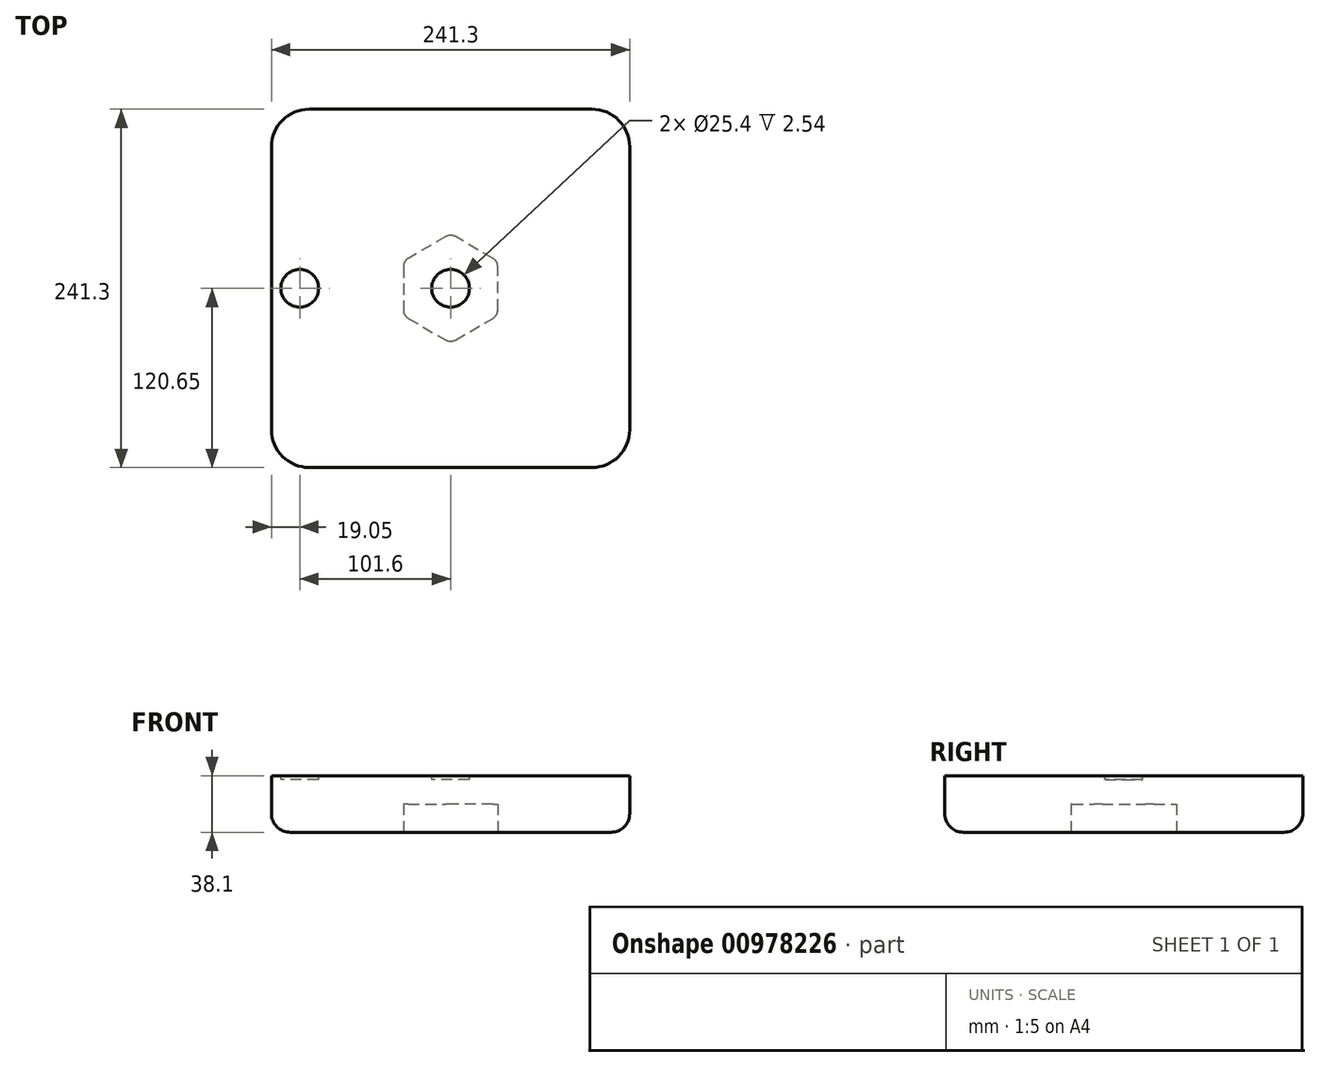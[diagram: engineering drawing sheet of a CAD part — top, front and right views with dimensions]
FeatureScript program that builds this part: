
annotation { "Feature Type Name" : "Feature", "Feature Type Description" : "" }
export const myFeature = defineFeature(function(context is Context, id is Id, definition is map)
    precondition{}
    {
        {
            var Q0;
            Q0=qCreatedBy(makeId("Top.planeOp"),FACE);
            var sketch = newSketch(context, id + "F0", { "sketchPlane" : qUnion([Q0])});
            skLineSegment(sketch, "E0.bottom", {"start": v(-120.65, 120.65) * mm, "end": v(120.65, 120.65) * mm});
            skLineSegment(sketch, "E0.top", {"start": v(-120.65, -120.65) * mm, "end": v(120.65, -120.65) * mm});
            skLineSegment(sketch, "E0.left", {"start": v(-120.65, 120.65) * mm, "end": v(-120.65, -120.65) * mm});
            skLineSegment(sketch, "E0.right", {"start": v(120.65, 120.65) * mm, "end": v(120.65, -120.65) * mm});
            skLineSegment(sketch, "E1", {"start": v(0, 0) * mm, "end": v(0, 120.65) * mm, "construction": true});
            skLineSegment(sketch, "E2", {"start": v(0, 0) * mm, "end": v(120.65, 0) * mm, "construction": true});
            skSolve(sketch);
        }
        {
            var Q0;
            Q0=makeQuery(id+"F0.imprint","IMPRINT",FACE,{"disambiguationData":[TD([[makeQuery(id+"F0.imprint","IMPRINT",EDGE,{"derivedFrom":sQuery(id+"F0.wireOp",EDGE,"E0.bottom")}),-1.0]])]});
            extrude(context, id + "F1", {"entities" : qUnion([Q0]), "oppositeDirection" : true, "depth" : 38.1 * mm, "offsetDistance" : 25.4 * mm});
        }
        {
            var Q0;
            Q0=makeQuery(id+"F1.opExtrude","SWEPT_EDGE",EDGE,{"disambiguationData":[OSD([sQuery(id+"F0.wireOp",EDGE,"E0.top"),sQuery(id+"F0.wireOp",EDGE,"E0.left")])]});
            var Q1;
            Q1=makeQuery(id+"F1.opExtrude","SWEPT_EDGE",EDGE,{"disambiguationData":[OSD([sQuery(id+"F0.wireOp",EDGE,"E0.bottom"),sQuery(id+"F0.wireOp",EDGE,"E0.left")])]});
            var Q2;
            Q2=makeQuery(id+"F1.opExtrude","SWEPT_EDGE",EDGE,{"disambiguationData":[OSD([sQuery(id+"F0.wireOp",EDGE,"E0.bottom"),sQuery(id+"F0.wireOp",EDGE,"E0.right")])]});
            var Q3;
            Q3=makeQuery(id+"F1.opExtrude","SWEPT_EDGE",EDGE,{"disambiguationData":[OSD([sQuery(id+"F0.wireOp",EDGE,"E0.top"),sQuery(id+"F0.wireOp",EDGE,"E0.right")])]});
            fillet(context, id + "F2", {"entities" : qUnion([Q0, Q1, Q2, Q3]), "radius" : 25.4 * mm, "tangentPropagation" : true, "allowEdgeOverflow" : false});
        }
        {
            var Q0;
            Q0=makeQuery(id+"F1.opExtrude","CAP_EDGE",EDGE,{"disambiguationData":[OSD([sQuery(id+"F0.wireOp",EDGE,"E0.top")])],"isStart":false});
            fillet(context, id + "F3", {"entities" : qUnion([Q0]), "radius" : 12.7 * mm, "tangentPropagation" : true, "allowEdgeOverflow" : false});
        }
        {
            var Q0;
            Q0=makeQuery(id+"F1.opExtrude","CAP_FACE",FACE,{"disambiguationData":[OSD([sQuery(id+"F0.wireOp",EDGE,"E0.bottom"),sQuery(id+"F0.wireOp",EDGE,"E0.top"),sQuery(id+"F0.wireOp",EDGE,"E0.left"),sQuery(id+"F0.wireOp",EDGE,"E0.right")])],"isStart":false});
            var sketch = newSketch(context, id + "F4", { "sketchPlane" : qUnion([Q0])});
            skCircle(sketch, "E3.cCircle", {"center": v(0, 0) * mm, "radius": 31.75 * mm, "construction": true});
            skLineSegment(sketch, "E3.0", {"start": v(-3.18, -34.83) * mm, "end": v(-28.57, -20.16) * mm});
            skLineSegment(sketch, "E3.1", {"start": v(-31.75, -14.66) * mm, "end": v(-31.75, 14.66) * mm});
            skLineSegment(sketch, "E3.2", {"start": v(-28.57, 20.16) * mm, "end": v(-3.17, 34.83) * mm});
            skLineSegment(sketch, "E3.3", {"start": v(3.18, 34.83) * mm, "end": v(28.58, 20.16) * mm});
            skLineSegment(sketch, "E3.4", {"start": v(31.75, 14.66) * mm, "end": v(31.75, -14.66) * mm});
            skLineSegment(sketch, "E3.5", {"start": v(28.58, -20.16) * mm, "end": v(3.17, -34.83) * mm});
            skPoint(sketch, "E3.0.midPoint", {"position": v(-15.88, -27.5) * mm});
            skPoint(sketch, "E4.visualSharp", {"position": v(0, 36.66) * mm});
            skArc(sketch, "E4.filletArc", {"start": v(3.18, 34.83) * mm, "mid": v(0, 35.68) * mm, "end": v(-3.17, 34.83) * mm});
            skPoint(sketch, "E5.visualSharp", {"position": v(31.75, 18.33) * mm});
            skArc(sketch, "E5.filletArc", {"start": v(31.75, 14.66) * mm, "mid": v(30.9, 17.84) * mm, "end": v(28.58, 20.16) * mm});
            skPoint(sketch, "E6.visualSharp", {"position": v(31.75, -18.33) * mm});
            skArc(sketch, "E6.filletArc", {"start": v(28.58, -20.16) * mm, "mid": v(30.9, -17.84) * mm, "end": v(31.75, -14.66) * mm});
            skPoint(sketch, "E7.visualSharp", {"position": v(0, -36.66) * mm});
            skArc(sketch, "E7.filletArc", {"start": v(-3.18, -34.83) * mm, "mid": v(0, -35.68) * mm, "end": v(3.17, -34.83) * mm});
            skPoint(sketch, "E8.visualSharp", {"position": v(-31.75, -18.33) * mm});
            skArc(sketch, "E8.filletArc", {"start": v(-31.75, -14.66) * mm, "mid": v(-30.9, -17.84) * mm, "end": v(-28.57, -20.16) * mm});
            skPoint(sketch, "E9.visualSharp", {"position": v(-31.75, 18.33) * mm});
            skArc(sketch, "E9.filletArc", {"start": v(-28.57, 20.16) * mm, "mid": v(-30.9, 17.84) * mm, "end": v(-31.75, 14.66) * mm});
            skSolve(sketch);
        }
        {
            var Q0;
            Q0 = qSketchRegion(id + "F4", true);
            extrude(context, id + "F5", {"entities" : qUnion([Q0]), "operationType" : NewBodyOperationType.REMOVE, "oppositeDirection" : true, "depth" : 19.05 * mm, "offsetDistance" : 25.4 * mm});
        }
        {
            var Q0;
            Q0=makeQuery(id+"F1.opExtrude","CAP_FACE",FACE,{"disambiguationData":[OSD([sQuery(id+"F0.wireOp",EDGE,"E0.bottom"),sQuery(id+"F0.wireOp",EDGE,"E0.top"),sQuery(id+"F0.wireOp",EDGE,"E0.left"),sQuery(id+"F0.wireOp",EDGE,"E0.right")])],"isStart":true});
            var sketch = newSketch(context, id + "F6", { "sketchPlane" : qUnion([Q0])});
            skCircle(sketch, "E10", {"center": v(-101.6, 0) * mm, "radius": 12.7 * mm});
            skSolve(sketch);
        }
        {
            var Q0;
            Q0=makeQuery(id+"F6.imprint","IMPRINT",FACE,{"disambiguationData":[TD([[makeQuery(id+"F6.imprint","IMPRINT",EDGE,{"derivedFrom":sQuery(id+"F6.wireOp",EDGE,"E10")}),1.0]])]});
            extrude(context, id + "F7", {"entities" : qUnion([Q0]), "operationType" : NewBodyOperationType.REMOVE, "oppositeDirection" : true, "depth" : 2.54 * mm, "offsetDistance" : 25.4 * mm});
        }
        {
            var Q0;
            Q0=makeQuery(id+"F1.opExtrude","CAP_FACE",FACE,{"disambiguationData":[OSD([sQuery(id+"F0.wireOp",EDGE,"E0.bottom"),sQuery(id+"F0.wireOp",EDGE,"E0.top"),sQuery(id+"F0.wireOp",EDGE,"E0.left"),sQuery(id+"F0.wireOp",EDGE,"E0.right")])],"isStart":true});
            var sketch = newSketch(context, id + "F8", { "sketchPlane" : qUnion([Q0])});
            skCircle(sketch, "E11", {"center": v(0, 0) * mm, "radius": 12.7 * mm});
            skSolve(sketch);
        }
        {
            var Q0;
            Q0 = qSketchRegion(id + "F8", true);
            extrude(context, id + "F9", {"entities" : qUnion([Q0]), "operationType" : NewBodyOperationType.REMOVE, "oppositeDirection" : true, "depth" : 2.54 * mm, "offsetDistance" : 25.4 * mm});
        }
    });
